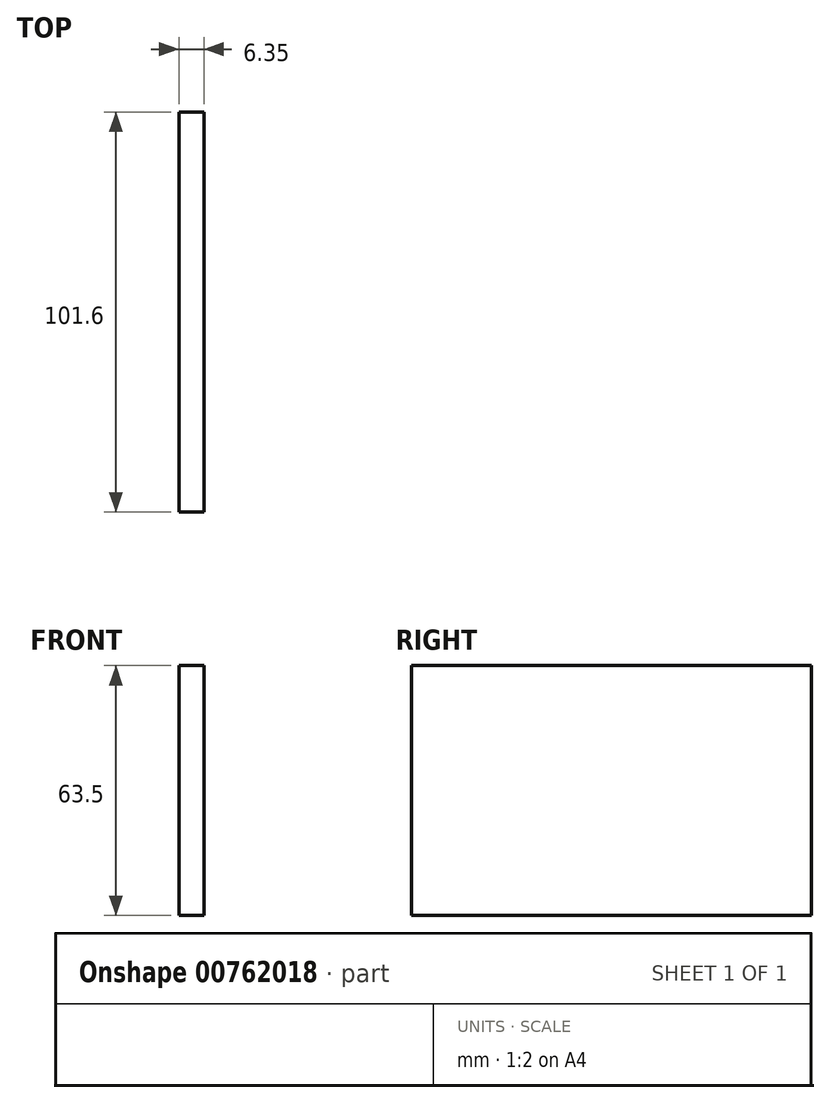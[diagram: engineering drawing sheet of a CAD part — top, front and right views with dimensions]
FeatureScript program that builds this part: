
annotation { "Feature Type Name" : "Feature", "Feature Type Description" : "" }
export const myFeature = defineFeature(function(context is Context, id is Id, definition is map)
    precondition{}
    {
        {
            var Q0;
            Q0=qCreatedBy(makeId("Right.planeOp"),FACE);
            var sketch = newSketch(context, id + "F0", { "sketchPlane" : qUnion([Q0])});
            skLineSegment(sketch, "E0", {"start": v(-49.78, 37.48) * mm, "end": v(51.82, 37.48) * mm});
            skLineSegment(sketch, "E1", {"start": v(-49.78, 37.48) * mm, "end": v(-49.78, -26.02) * mm});
            skLineSegment(sketch, "E2", {"start": v(51.82, 37.48) * mm, "end": v(51.82, -26.02) * mm});
            skLineSegment(sketch, "E3", {"start": v(51.82, -26.02) * mm, "end": v(-49.78, -26.02) * mm});
            skSolve(sketch);
        }
        {
            var Q0;
            Q0=makeQuery(id+"F0.imprint","IMPRINT",FACE,{"disambiguationData":[TD([[makeQuery(id+"F0.imprint","IMPRINT",EDGE,{"derivedFrom":sQuery(id+"F0.wireOp",EDGE,"E0")}),-1.0]])]});
            extrude(context, id + "F1", {"entities" : qUnion([Q0]), "depth" : 6.35 * mm, "offsetDistance" : 25.4 * mm});
        }
    });
